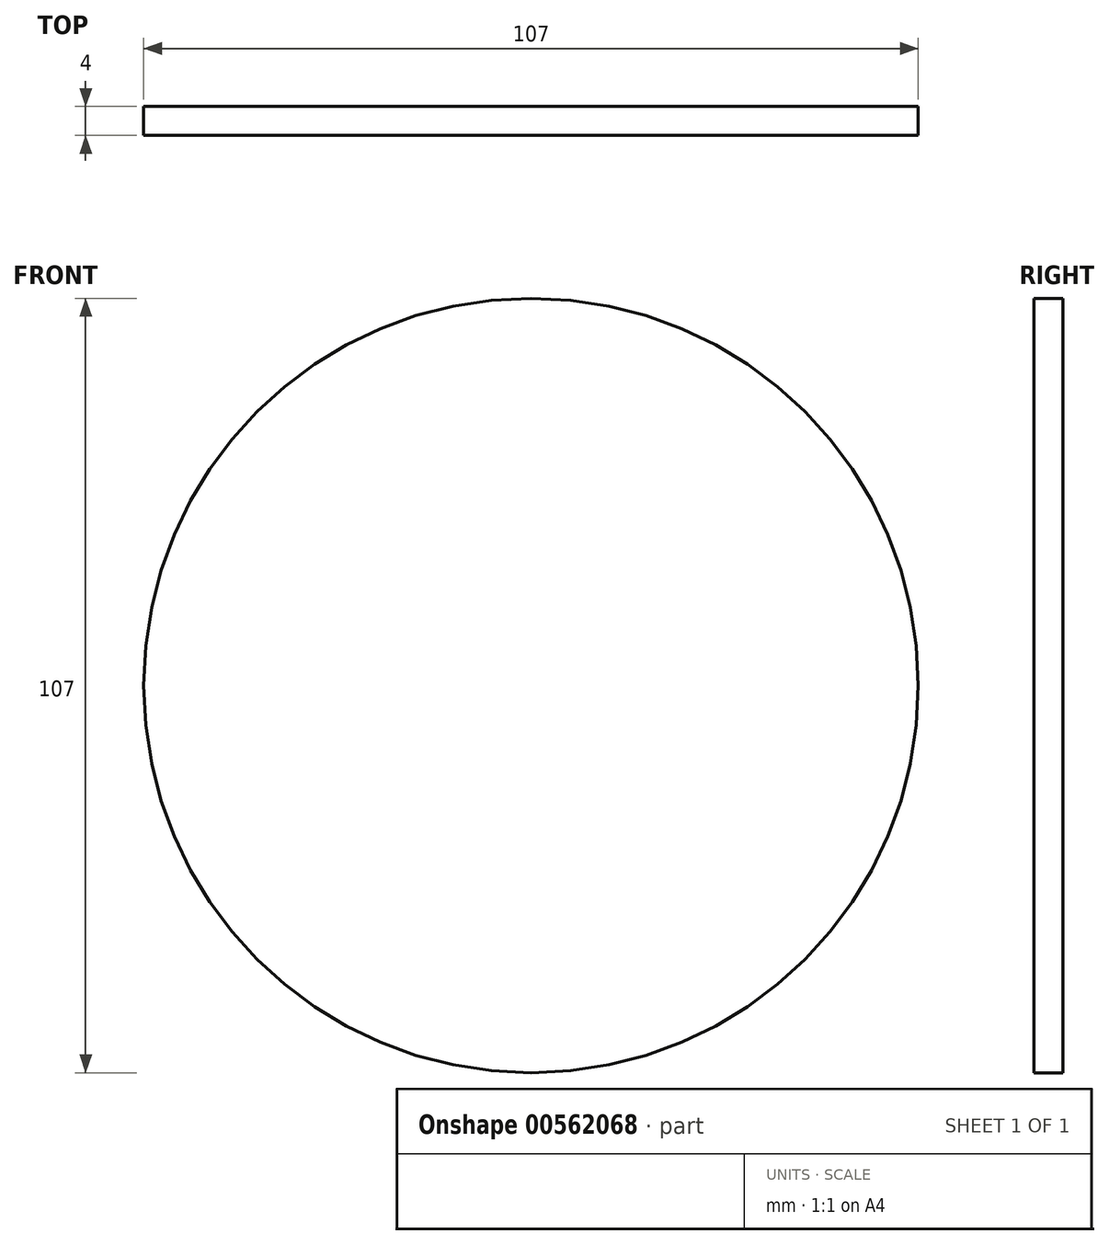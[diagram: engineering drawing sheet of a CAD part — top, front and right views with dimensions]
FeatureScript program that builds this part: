
annotation { "Feature Type Name" : "Feature", "Feature Type Description" : "" }
export const myFeature = defineFeature(function(context is Context, id is Id, definition is map)
    precondition{}
    {
        {
            var Q0;
            Q0=qCreatedBy(makeId("Front.planeOp"),FACE);
            var sketch = newSketch(context, id + "F0", { "sketchPlane" : qUnion([Q0])});
            skCircle(sketch, "E0", {"center": v(0, 0) * mm, "radius": 53.5 * mm});
            skSolve(sketch);
        }
        {
            var Q0;
            Q0=makeQuery(id+"F0.imprint","IMPRINT",FACE,{"disambiguationData":[TD([[makeQuery(id+"F0.imprint","IMPRINT",EDGE,{"derivedFrom":sQuery(id+"F0.wireOp",EDGE,"E0")}),1.0]])]});
            extrude(context, id + "F1", {"entities" : qUnion([Q0]), "depth" : 4 * mm, "offsetDistance" : 25 * mm});
        }
    });
